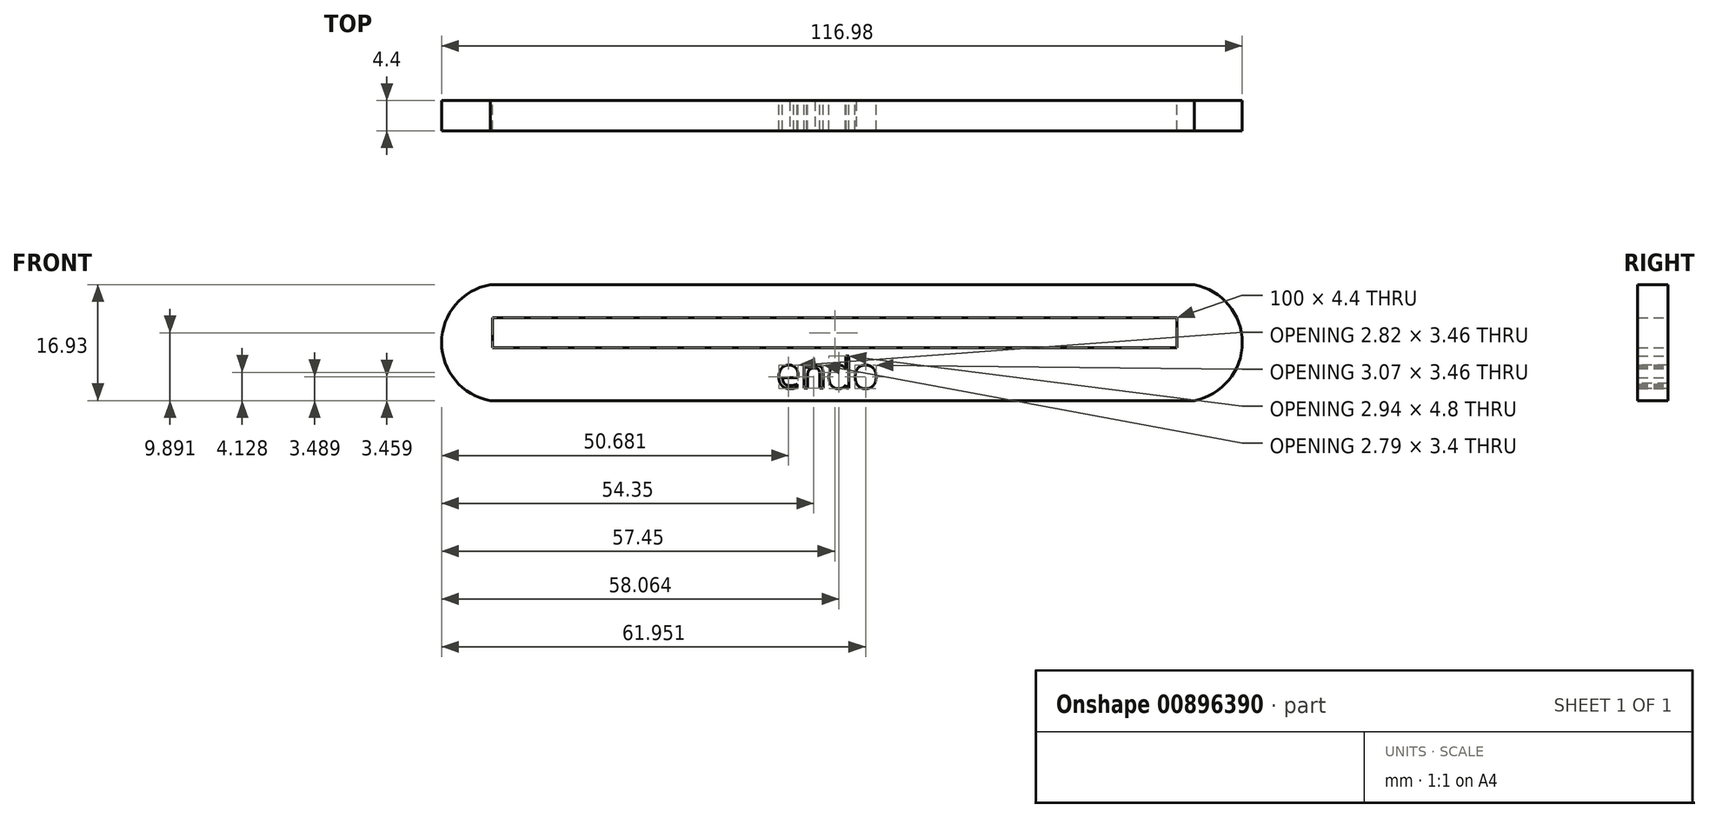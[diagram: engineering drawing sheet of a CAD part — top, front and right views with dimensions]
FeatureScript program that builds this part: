
annotation { "Feature Type Name" : "Feature", "Feature Type Description" : "" }
export const myFeature = defineFeature(function(context is Context, id is Id, definition is map)
    precondition{}
    {
        {
            var Q0;
            Q0=qCreatedBy(makeId("Front.planeOp"),FACE);
            var sketch = newSketch(context, id + "F0", { "sketchPlane" : qUnion([Q0])});
            skLineSegment(sketch, "E0", {"start": v(-14.37, 19.8) * mm, "end": v(-12.84, 20.5) * mm});
            skLineSegment(sketch, "E1", {"start": v(-12.84, 20.5) * mm, "end": v(-11.5, 21.11) * mm});
            skLineSegment(sketch, "E2", {"start": v(-11.5, 21.11) * mm, "end": v(-9.6, 21.92) * mm});
            skLineSegment(sketch, "E3", {"start": v(-9.6, 21.92) * mm, "end": v(-7.78, 22.67) * mm});
            skLineSegment(sketch, "E4", {"start": v(-7.78, 22.67) * mm, "end": v(-5.32, 23.36) * mm});
            skLineSegment(sketch, "E5", {"start": v(-5.32, 23.36) * mm, "end": v(-3.2, 23.87) * mm});
            skLineSegment(sketch, "E6", {"start": v(-3.2, 23.87) * mm, "end": v(-0.6, 24.35) * mm});
            skLineSegment(sketch, "E7", {"start": v(-0.6, 24.35) * mm, "end": v(1.8, 24.68) * mm});
            skLineSegment(sketch, "E8", {"start": v(1.8, 24.68) * mm, "end": v(4.06, 24.68) * mm});
            skLineSegment(sketch, "E9", {"start": v(4.06, 24.68) * mm, "end": v(6.76, 24.92) * mm});
            skLineSegment(sketch, "E10", {"start": v(6.76, 24.92) * mm, "end": v(9.3, 24.92) * mm});
            skLineSegment(sketch, "E11", {"start": v(9.3, 24.92) * mm, "end": v(10.16, 24.92) * mm});
            skLineSegment(sketch, "E12", {"start": v(10.16, 24.92) * mm, "end": v(11.26, 24.92) * mm});
            skLineSegment(sketch, "E13", {"start": v(11.26, 24.92) * mm, "end": v(13.38, 24.6) * mm});
            skLineSegment(sketch, "E14", {"start": v(13.38, 24.6) * mm, "end": v(14.76, 24.3) * mm});
            skLineSegment(sketch, "E15", {"start": v(-6.2, 22.67) * mm, "end": v(-4, 20.8) * mm});
            skLineSegment(sketch, "E16", {"start": v(-4, 20.8) * mm, "end": v(-1.58, 18.38) * mm});
            skLineSegment(sketch, "E17", {"start": v(-1.58, 18.38) * mm, "end": v(0.62, 16.02) * mm});
            skLineSegment(sketch, "E18", {"start": v(0.62, 16.02) * mm, "end": v(3.16, 12.97) * mm});
            skLineSegment(sketch, "E19", {"start": v(3.16, 12.97) * mm, "end": v(5.46, 10) * mm});
            skLineSegment(sketch, "E20", {"start": v(5.46, 10) * mm, "end": v(1.36, 6.83) * mm});
            skLineSegment(sketch, "E21", {"start": v(1.36, 6.83) * mm, "end": v(-1.17, 4.9) * mm});
            skLineSegment(sketch, "E22", {"start": v(-1.17, 4.9) * mm, "end": v(-3.62, 3.1) * mm});
            skLineSegment(sketch, "E23", {"start": v(-3.62, 3.1) * mm, "end": v(-5.05, 2.17) * mm});
            skLineSegment(sketch, "E24", {"start": v(-5.05, 2.17) * mm, "end": v(-6.42, 1.76) * mm});
            skLineSegment(sketch, "E25", {"start": v(-6.42, 1.76) * mm, "end": v(-8.2, 1.4) * mm});
            skLineSegment(sketch, "E26", {"start": v(-8.2, 1.4) * mm, "end": v(-9.92, 1.4) * mm});
            skLineSegment(sketch, "E27", {"start": v(-9.92, 1.4) * mm, "end": v(-11.61, 2.17) * mm});
            skLineSegment(sketch, "E28", {"start": v(-11.61, 2.17) * mm, "end": v(-13.71, 3.28) * mm});
            skLineSegment(sketch, "E29", {"start": v(-13.71, 3.28) * mm, "end": v(-15.08, 4.24) * mm});
            skLineSegment(sketch, "E30", {"start": v(-15.08, 4.24) * mm, "end": v(-16.23, 5.16) * mm});
            skLineSegment(sketch, "E31", {"start": v(-16.23, 5.16) * mm, "end": v(-17.57, 6.44) * mm});
            skLineSegment(sketch, "E32", {"start": v(-17.57, 6.44) * mm, "end": v(-18.97, 8.25) * mm});
            skLineSegment(sketch, "E33", {"start": v(-18.97, 8.25) * mm, "end": v(-19.8, 10.26) * mm});
            skLineSegment(sketch, "E34", {"start": v(-19.8, 10.26) * mm, "end": v(-20.4, 12.58) * mm});
            skLineSegment(sketch, "E35", {"start": v(-20.4, 12.58) * mm, "end": v(-20.4, 14.43) * mm});
            skLineSegment(sketch, "E36", {"start": v(-20.4, 14.43) * mm, "end": v(-20.4, 15.39) * mm});
            skLineSegment(sketch, "E37", {"start": v(-20.4, 15.39) * mm, "end": v(-20.4, 15.77) * mm});
            skLineSegment(sketch, "E38", {"start": v(-20.4, 15.77) * mm, "end": v(-19.8, 16.21) * mm});
            skLineSegment(sketch, "E39", {"start": v(-19.8, 16.21) * mm, "end": v(-19.22, 16.66) * mm});
            skLineSegment(sketch, "E40", {"start": v(-19.22, 16.66) * mm, "end": v(-18.59, 17.1) * mm});
            skLineSegment(sketch, "E41", {"start": v(-18.59, 17.1) * mm, "end": v(-17.66, 17.62) * mm});
            skLineSegment(sketch, "E42", {"start": v(-17.66, 17.62) * mm, "end": v(-16.26, 18.41) * mm});
            skLineSegment(sketch, "E43", {"start": v(-16.26, 18.41) * mm, "end": v(-14.37, 19.4) * mm});
            skLineSegment(sketch, "E44", {"start": v(-14.37, 19.4) * mm, "end": v(-9.64, 21.53) * mm});
            skLineSegment(sketch, "E45", {"start": v(-9.64, 21.53) * mm, "end": v(-8.2, 22.19) * mm});
            skLineSegment(sketch, "E46", {"start": v(-8.2, 22.19) * mm, "end": v(-6.49, 22.71) * mm});
            skLineSegment(sketch, "E47", {"start": v(-6.49, 22.71) * mm, "end": v(-6.2, 22.67) * mm});
            skLineSegment(sketch, "E48", {"start": v(-14.37, 19.8) * mm, "end": v(-15.76, 19.8) * mm});
            skLineSegment(sketch, "E49", {"start": v(-15.76, 19.8) * mm, "end": v(-18.48, 20.24) * mm});
            skLineSegment(sketch, "E50", {"start": v(-18.48, 20.24) * mm, "end": v(-19.61, 20.24) * mm});
            skLineSegment(sketch, "E51", {"start": v(-19.61, 20.24) * mm, "end": v(-21.2, 20.24) * mm});
            skLineSegment(sketch, "E52", {"start": v(-21.2, 20.24) * mm, "end": v(-22.72, 20.24) * mm});
            skLineSegment(sketch, "E53", {"start": v(-22.72, 20.24) * mm, "end": v(-24.16, 20) * mm});
            skLineSegment(sketch, "E54", {"start": v(-24.16, 20) * mm, "end": v(-25.7, 19.62) * mm});
            skLineSegment(sketch, "E55", {"start": v(-25.7, 19.62) * mm, "end": v(-27.35, 19.03) * mm});
            skLineSegment(sketch, "E56", {"start": v(-27.35, 19.03) * mm, "end": v(-29.07, 18.04) * mm});
            skLineSegment(sketch, "E57", {"start": v(-29.07, 18.04) * mm, "end": v(-30.32, 17.21) * mm});
            skLineSegment(sketch, "E58", {"start": v(-30.32, 17.21) * mm, "end": v(-31.56, 16.22) * mm});
            skLineSegment(sketch, "E59", {"start": v(-31.56, 16.22) * mm, "end": v(-32.9, 14.85) * mm});
            skLineSegment(sketch, "E60", {"start": v(-32.9, 14.85) * mm, "end": v(-34.29, 13.33) * mm});
            skLineSegment(sketch, "E61", {"start": v(-34.29, 13.33) * mm, "end": v(-35.55, 11.64) * mm});
            skLineSegment(sketch, "E62", {"start": v(-26.63, 12.1) * mm, "end": v(-27.14, 11.27) * mm});
            skLineSegment(sketch, "E63", {"start": v(-27.14, 11.27) * mm, "end": v(-27.86, 8.61) * mm});
            skLineSegment(sketch, "E64", {"start": v(-27.86, 8.61) * mm, "end": v(-27.86, 8.33) * mm});
            skLineSegment(sketch, "E65", {"start": v(-27.86, 8.33) * mm, "end": v(-26.42, 12.22) * mm});
            skLineSegment(sketch, "E66", {"start": v(-26.42, 12.22) * mm, "end": v(-26.63, 12.1) * mm});
            skLineSegment(sketch, "E67", {"start": v(-35.55, 11.64) * mm, "end": v(-37.65, 8.82) * mm});
            skLineSegment(sketch, "E68", {"start": v(-37.65, 8.82) * mm, "end": v(-38.58, 6.3) * mm});
            skLineSegment(sketch, "E69", {"start": v(-38.58, 6.3) * mm, "end": v(-39.61, 3.52) * mm});
            skLineSegment(sketch, "E70", {"start": v(-39.61, 3.52) * mm, "end": v(-40.12, -3.45) * mm});
            skLineSegment(sketch, "E71", {"start": v(-40.12, -3.45) * mm, "end": v(-36.66, -6.6) * mm});
            skLineSegment(sketch, "E72", {"start": v(-36.66, -6.6) * mm, "end": v(-31.38, -11.2) * mm});
            skLineSegment(sketch, "E73", {"start": v(-31.38, -11.2) * mm, "end": v(-29.18, -12.85) * mm});
            skLineSegment(sketch, "E74", {"start": v(-19.8, -1.41) * mm, "end": v(-23.14, 0) * mm});
            skLineSegment(sketch, "E75", {"start": v(-23.14, 0) * mm, "end": v(-23.14, 0.57) * mm});
            skLineSegment(sketch, "E76", {"start": v(-23.14, 0.57) * mm, "end": v(-18.73, -1.14) * mm});
            skLineSegment(sketch, "E77", {"start": v(-18.73, -1.14) * mm, "end": v(-19.8, -1.41) * mm});
            skLineSegment(sketch, "E78", {"start": v(-31.56, 16.22) * mm, "end": v(-32.59, 13.43) * mm});
            skLineSegment(sketch, "E79", {"start": v(-32.59, 13.43) * mm, "end": v(-37.24, 8.1) * mm});
            skLineSegment(sketch, "E80", {"start": v(-37.24, 8.1) * mm, "end": v(-36.3, 10.64) * mm});
            skLineSegment(sketch, "E81", {"start": v(-28.86, -9.02) * mm, "end": v(-27.82, -8.4) * mm});
            skLineSegment(sketch, "E82", {"start": v(-27.82, -8.4) * mm, "end": v(-25.66, -7.72) * mm});
            skLineSegment(sketch, "E83", {"start": v(-25.66, -7.72) * mm, "end": v(-22.42, -6.86) * mm});
            skLineSegment(sketch, "E84", {"start": v(-22.42, -6.86) * mm, "end": v(-21.78, -6.63) * mm});
            skLineSegment(sketch, "E85", {"start": v(-21.78, -6.63) * mm, "end": v(-20.96, -6.63) * mm});
            skLineSegment(sketch, "E86", {"start": v(-20.96, -6.63) * mm, "end": v(-20.22, -6.8) * mm});
            skLineSegment(sketch, "E87", {"start": v(-20.22, -6.8) * mm, "end": v(-18.78, -7.38) * mm});
            skLineSegment(sketch, "E88", {"start": v(-18.78, -7.38) * mm, "end": v(-21.57, -9.34) * mm});
            skLineSegment(sketch, "E89", {"start": v(-21.57, -9.34) * mm, "end": v(-22.56, -9.9) * mm});
            skLineSegment(sketch, "E90", {"start": v(-22.56, -9.9) * mm, "end": v(-23.64, -10.29) * mm});
            skLineSegment(sketch, "E91", {"start": v(-23.64, -10.29) * mm, "end": v(-24.72, -10.5) * mm});
            skLineSegment(sketch, "E92", {"start": v(-24.72, -10.5) * mm, "end": v(-25.8, -10.5) * mm});
            skLineSegment(sketch, "E93", {"start": v(-25.8, -10.5) * mm, "end": v(-28.52, -9.42) * mm});
            skLineSegment(sketch, "E94", {"start": v(-28.52, -9.42) * mm, "end": v(-28.86, -9.02) * mm});
            skLineSegment(sketch, "E95", {"start": v(-36.66, -6.6) * mm, "end": v(-36.3, -7.81) * mm});
            skLineSegment(sketch, "E96", {"start": v(-36.3, -7.81) * mm, "end": v(-35.69, -9.02) * mm});
            skLineSegment(sketch, "E97", {"start": v(-35.69, -9.02) * mm, "end": v(-34, -11) * mm});
            skLineSegment(sketch, "E98", {"start": v(-34, -11) * mm, "end": v(-32.11, -12.4) * mm});
            skLineSegment(sketch, "E99", {"start": v(-32.11, -12.4) * mm, "end": v(-30.96, -13.41) * mm});
            skLineSegment(sketch, "E100", {"start": v(-30.96, -13.41) * mm, "end": v(-31.96, -14.75) * mm});
            skLineSegment(sketch, "E101", {"start": v(-31.96, -14.75) * mm, "end": v(-30.67, -16.2) * mm});
            skLineSegment(sketch, "E102", {"start": v(-30.67, -16.2) * mm, "end": v(-29.38, -17.22) * mm});
            skLineSegment(sketch, "E103", {"start": v(-29.38, -17.22) * mm, "end": v(-27.98, -18.01) * mm});
            skLineSegment(sketch, "E104", {"start": v(-27.98, -18.01) * mm, "end": v(-27.75, -18.37) * mm});
            skLineSegment(sketch, "E105", {"start": v(-27.75, -18.37) * mm, "end": v(-26.52, -18.74) * mm});
            skLineSegment(sketch, "E106", {"start": v(-26.52, -18.74) * mm, "end": v(-22.5, -19.28) * mm});
            skLineSegment(sketch, "E107", {"start": v(-22.5, -19.28) * mm, "end": v(-20.23, -19.28) * mm});
            skLineSegment(sketch, "E108", {"start": v(-20.23, -19.28) * mm, "end": v(-18.05, -19.28) * mm});
            skLineSegment(sketch, "E109", {"start": v(-18.05, -19.28) * mm, "end": v(-17.55, -19.64) * mm});
            skLineSegment(sketch, "E110", {"start": v(-17.55, -19.64) * mm, "end": v(-16.56, -19.64) * mm});
            skLineSegment(sketch, "E111", {"start": v(-16.56, -19.64) * mm, "end": v(-16.56, -18.01) * mm});
            skLineSegment(sketch, "E112", {"start": v(-16.56, -18.01) * mm, "end": v(-16.36, -18.01) * mm});
            skLineSegment(sketch, "E113", {"start": v(-16.36, -18.01) * mm, "end": v(-15.69, -19) * mm});
            skLineSegment(sketch, "E114", {"start": v(-15.69, -19) * mm, "end": v(-14.87, -19.93) * mm});
            skLineSegment(sketch, "E115", {"start": v(-14.87, -19.93) * mm, "end": v(-14, -20.56) * mm});
            skLineSegment(sketch, "E116", {"start": v(-14, -20.56) * mm, "end": v(-13.34, -20.97) * mm});
            skLineSegment(sketch, "E117", {"start": v(-13.34, -20.97) * mm, "end": v(-12.71, -21.2) * mm});
            skLineSegment(sketch, "E118", {"start": v(-12.71, -21.2) * mm, "end": v(-11.38, -21.44) * mm});
            skLineSegment(sketch, "E119", {"start": v(-11.38, -21.44) * mm, "end": v(-9.9, -21.44) * mm});
            skLineSegment(sketch, "E120", {"start": v(-9.9, -21.44) * mm, "end": v(-8.37, -20.88) * mm});
            skLineSegment(sketch, "E121", {"start": v(-8.37, -20.88) * mm, "end": v(-7.4, -20.54) * mm});
            skLineSegment(sketch, "E122", {"start": v(-7.4, -20.54) * mm, "end": v(-6.02, -19.93) * mm});
            skLineSegment(sketch, "E123", {"start": v(-6.02, -19.93) * mm, "end": v(-4.94, -19.28) * mm});
            skLineSegment(sketch, "E124", {"start": v(-4.94, -19.28) * mm, "end": v(-3.95, -18.42) * mm});
            skLineSegment(sketch, "E125", {"start": v(-3.95, -18.42) * mm, "end": v(-2.83, -17.5) * mm});
            skLineSegment(sketch, "E126", {"start": v(-2.83, -17.5) * mm, "end": v(-1.97, -16.71) * mm});
            skLineSegment(sketch, "E127", {"start": v(-1.97, -16.71) * mm, "end": v(-1.12, -15.74) * mm});
            skLineSegment(sketch, "E128", {"start": v(-1.12, -15.74) * mm, "end": v(-0.48, -14.75) * mm});
            skLineSegment(sketch, "E129", {"start": v(-0.48, -14.75) * mm, "end": v(0.21, -13.06) * mm});
            skLineSegment(sketch, "E130", {"start": v(0.21, -13.06) * mm, "end": v(0.21, -11.98) * mm});
            skLineSegment(sketch, "E131", {"start": v(0.21, -11.98) * mm, "end": v(0.15, -10.97) * mm});
            skLineSegment(sketch, "E132", {"start": v(0.15, -10.97) * mm, "end": v(-0.3, -10.05) * mm});
            skLineSegment(sketch, "E133", {"start": v(-0.3, -10.05) * mm, "end": v(-1.1, -9.75) * mm});
            skLineSegment(sketch, "E134", {"start": v(-1.1, -9.75) * mm, "end": v(-2.3, -9.5) * mm});
            skLineSegment(sketch, "E135", {"start": v(-2.3, -9.5) * mm, "end": v(-4.02, -9.5) * mm});
            skLineSegment(sketch, "E136", {"start": v(-4.02, -9.5) * mm, "end": v(-5.46, -9.87) * mm});
            skLineSegment(sketch, "E137", {"start": v(-5.46, -9.87) * mm, "end": v(-6.9, -10.4) * mm});
            skLineSegment(sketch, "E138", {"start": v(-6.9, -10.4) * mm, "end": v(-7.96, -11.01) * mm});
            skLineSegment(sketch, "E139", {"start": v(-7.96, -11.01) * mm, "end": v(-9.09, -11.62) * mm});
            skLineSegment(sketch, "E140", {"start": v(-9.09, -11.62) * mm, "end": v(-10.06, -12.39) * mm});
            skLineSegment(sketch, "E141", {"start": v(-10.06, -12.39) * mm, "end": v(-10.98, -13.27) * mm});
            skLineSegment(sketch, "E142", {"start": v(-10.98, -13.27) * mm, "end": v(-12.3, -14.98) * mm});
            skLineSegment(sketch, "E143", {"start": v(-12.3, -14.98) * mm, "end": v(-13.1, -16.35) * mm});
            skLineSegment(sketch, "E144", {"start": v(-13.1, -16.35) * mm, "end": v(-13.6, -18.42) * mm});
            skLineSegment(sketch, "E145", {"start": v(-13.6, -18.42) * mm, "end": v(-12.83, -20.76) * mm});
            skLineSegment(sketch, "E146", {"start": v(-12.83, -20.76) * mm, "end": v(-11.38, -21.44) * mm});
            skLineSegment(sketch, "E147", {"start": v(-16.36, -18.01) * mm, "end": v(-16.07, -16.45) * mm});
            skLineSegment(sketch, "E148", {"start": v(-16.07, -16.45) * mm, "end": v(-15, -14.75) * mm});
            skLineSegment(sketch, "E149", {"start": v(-15, -14.75) * mm, "end": v(-13.73, -13.56) * mm});
            skLineSegment(sketch, "E150", {"start": v(-13.73, -13.56) * mm, "end": v(-12.66, -12.83) * mm});
            skLineSegment(sketch, "E151", {"start": v(-12.66, -12.83) * mm, "end": v(-11.38, -11.97) * mm});
            skLineSegment(sketch, "E152", {"start": v(-11.38, -11.97) * mm, "end": v(-10.42, -11.31) * mm});
            skLineSegment(sketch, "E153", {"start": v(-10.42, -11.31) * mm, "end": v(-8.78, -10.2) * mm});
            skLineSegment(sketch, "E154", {"start": v(-8.78, -10.2) * mm, "end": v(-6.81, -9.41) * mm});
            skLineSegment(sketch, "E155", {"start": v(-6.81, -9.41) * mm, "end": v(-5.1, -8.8) * mm});
            skLineSegment(sketch, "E156", {"start": v(-5.1, -8.8) * mm, "end": v(-3.2, -8.1) * mm});
            skLineSegment(sketch, "E157", {"start": v(-3.2, -8.1) * mm, "end": v(-1.86, -7.84) * mm});
            skLineSegment(sketch, "E158", {"start": v(-1.86, -7.84) * mm, "end": v(0, -8.18) * mm});
            skLineSegment(sketch, "E159", {"start": v(0, -8.18) * mm, "end": v(1.43, -9.4) * mm});
            skLineSegment(sketch, "E160", {"start": v(1.43, -9.4) * mm, "end": v(1.63, -10.81) * mm});
            skLineSegment(sketch, "E161", {"start": v(1.63, -10.81) * mm, "end": v(1.9, -12.86) * mm});
            skLineSegment(sketch, "E162", {"start": v(1.9, -12.86) * mm, "end": v(1.55, -14.75) * mm});
            skLineSegment(sketch, "E163", {"start": v(1.55, -14.75) * mm, "end": v(0.31, -12.93) * mm});
            skLineSegment(sketch, "E164", {"start": v(-14, -13.8) * mm, "end": v(-17.21, -14.02) * mm});
            skPoint(sketch, "E164.startSnap0", {"position": v(1.73, -13.8) * mm});
            skLineSegment(sketch, "E165", {"start": v(-17.21, -14.02) * mm, "end": v(-16.18, -13.06) * mm});
            skLineSegment(sketch, "E166", {"start": v(-16.18, -13.06) * mm, "end": v(-14.94, -12.22) * mm});
            skLineSegment(sketch, "E167", {"start": v(-14.94, -12.22) * mm, "end": v(-13.32, -11.01) * mm});
            skLineSegment(sketch, "E168", {"start": v(-13.32, -11.01) * mm, "end": v(-11.5, -10.08) * mm});
            skLineSegment(sketch, "E169", {"start": v(-11.5, -10.08) * mm, "end": v(-8.6, -8.98) * mm});
            skLineSegment(sketch, "E170", {"start": v(-32.03, -10.64) * mm, "end": v(-29.73, -14.32) * mm});
            skLineSegment(sketch, "E171", {"start": v(-29.73, -14.32) * mm, "end": v(-28.15, -16.14) * mm});
            skLineSegment(sketch, "E172", {"start": v(-28.15, -16.14) * mm, "end": v(-26.63, -17.27) * mm});
            skLineSegment(sketch, "E173", {"start": v(-26.63, -17.27) * mm, "end": v(-24.35, -17.96) * mm});
            skLineSegment(sketch, "E174", {"start": v(-24.35, -17.96) * mm, "end": v(-22.04, -17.96) * mm});
            skLineSegment(sketch, "E175", {"start": v(-22.04, -17.96) * mm, "end": v(-20.52, -17.96) * mm});
            skLineSegment(sketch, "E176", {"start": v(-20.52, -17.96) * mm, "end": v(-20.52, -18.15) * mm});
            skLineSegment(sketch, "E177", {"start": v(-20.52, -18.15) * mm, "end": v(-19.92, -18.15) * mm});
            skLineSegment(sketch, "E178", {"start": v(-19.92, -18.15) * mm, "end": v(-19.92, -17.96) * mm});
            skLineSegment(sketch, "E179", {"start": v(-19.92, -17.96) * mm, "end": v(-16.6, -17.32) * mm});
            skLineSegment(sketch, "E180", {"start": v(-16.6, -17.32) * mm, "end": v(-16.36, -18.01) * mm});
            skLineSegment(sketch, "E181", {"start": v(-20.96, -17.96) * mm, "end": v(-16.68, -16.83) * mm});
            skLineSegment(sketch, "E182", {"start": v(-16.68, -16.83) * mm, "end": v(-16.36, -16.4) * mm});
            skLineSegment(sketch, "E183", {"start": v(-16.36, -16.4) * mm, "end": v(-21.8, -16.4) * mm});
            skLineSegment(sketch, "E184", {"start": v(-21.8, -16.4) * mm, "end": v(-22.7, -15.73) * mm});
            skLineSegment(sketch, "E185", {"start": v(-22.7, -15.73) * mm, "end": v(-23.12, -15.35) * mm});
            skLineSegment(sketch, "E186", {"start": v(-23.12, -15.35) * mm, "end": v(-26.1, -14.33) * mm});
            skLineSegment(sketch, "E187", {"start": v(-26.1, -14.33) * mm, "end": v(-29.18, -12.85) * mm});
            skLineSegment(sketch, "E188", {"start": v(-8.6, -8.98) * mm, "end": v(-5.7, -7.8) * mm});
            skLineSegment(sketch, "E189", {"start": v(-5.7, -7.8) * mm, "end": v(-3.24, -7.46) * mm});
            skLineSegment(sketch, "E190", {"start": v(-3.24, -7.46) * mm, "end": v(-1.9, -7.27) * mm});
            skLineSegment(sketch, "E191", {"start": v(-1.9, -7.27) * mm, "end": v(-0.26, -7.54) * mm});
            skLineSegment(sketch, "E192", {"start": v(-0.26, -7.54) * mm, "end": v(0.82, -8.26) * mm});
            skLineSegment(sketch, "E193", {"start": v(0.82, -8.26) * mm, "end": v(1.5, -8.98) * mm});
            skLineSegment(sketch, "E194", {"start": v(1.5, -8.98) * mm, "end": v(1.8, -9.9) * mm});
            skLineSegment(sketch, "E195", {"start": v(1.8, -9.9) * mm, "end": v(1.98, -11.15) * mm});
            skLineSegment(sketch, "E196", {"start": v(1.98, -11.15) * mm, "end": v(2.26, -13.1) * mm});
            skLineSegment(sketch, "E197", {"start": v(2.26, -13.1) * mm, "end": v(3.74, -12.35) * mm});
            skLineSegment(sketch, "E198", {"start": v(3.74, -12.35) * mm, "end": v(6.12, -11.05) * mm});
            skLineSegment(sketch, "E199", {"start": v(6.12, -11.05) * mm, "end": v(9.27, -9.5) * mm});
            skLineSegment(sketch, "E200", {"start": v(9.27, -9.5) * mm, "end": v(18.37, -5.74) * mm});
            skLineSegment(sketch, "E201", {"start": v(18.37, -5.74) * mm, "end": v(21.69, -4.65) * mm});
            skLineSegment(sketch, "E202", {"start": v(1.55, -14.75) * mm, "end": v(8.6, -11.67) * mm});
            skLineSegment(sketch, "E203", {"start": v(8.6, -11.67) * mm, "end": v(14.4, -9.55) * mm});
            skLineSegment(sketch, "E204", {"start": v(14.4, -9.55) * mm, "end": v(20, -8.02) * mm});
            skLineSegment(sketch, "E205", {"start": v(20, -8.02) * mm, "end": v(26.3, -6.44) * mm});
            skLineSegment(sketch, "E206", {"start": v(26.3, -6.44) * mm, "end": v(28.09, -6.44) * mm});
            skLineSegment(sketch, "E207", {"start": v(28.09, -6.44) * mm, "end": v(28.53, -5.36) * mm});
            skLineSegment(sketch, "E208", {"start": v(-1.91, 1.26) * mm, "end": v(-0.42, 3) * mm});
            skLineSegment(sketch, "E209", {"start": v(-0.42, 3) * mm, "end": v(1.47, 4.76) * mm});
            skLineSegment(sketch, "E210", {"start": v(1.47, 4.76) * mm, "end": v(2.7, 5.96) * mm});
            skLineSegment(sketch, "E211", {"start": v(2.7, 5.96) * mm, "end": v(4.14, 7) * mm});
            skLineSegment(sketch, "E212", {"start": v(4.14, 7) * mm, "end": v(7.13, 8.84) * mm});
            skLineSegment(sketch, "E213", {"start": v(7.13, 8.84) * mm, "end": v(9.78, 10.12) * mm});
            skLineSegment(sketch, "E214", {"start": v(9.78, 10.12) * mm, "end": v(12.36, 11.01) * mm});
            skLineSegment(sketch, "E215", {"start": v(12.36, 11.01) * mm, "end": v(14.35, 11.54) * mm});
            skLineSegment(sketch, "E216", {"start": v(14.35, 11.54) * mm, "end": v(16.1, 11.85) * mm});
            skLineSegment(sketch, "E217", {"start": v(16.1, 11.85) * mm, "end": v(17.72, 12.17) * mm});
            skLineSegment(sketch, "E218", {"start": v(17.72, 12.17) * mm, "end": v(19.92, 12.17) * mm});
            skLineSegment(sketch, "E219", {"start": v(19.92, 12.17) * mm, "end": v(22, 12.17) * mm});
            skLineSegment(sketch, "E220", {"start": v(22, 12.17) * mm, "end": v(23.46, 12.17) * mm});
            skLineSegment(sketch, "E221", {"start": v(23.46, 12.17) * mm, "end": v(25.1, 12.17) * mm});
            skLineSegment(sketch, "E222", {"start": v(25.1, 12.17) * mm, "end": v(26.96, 11.6) * mm});
            skLineSegment(sketch, "E223", {"start": v(26.96, 11.6) * mm, "end": v(26.14, 10.78) * mm});
            skLineSegment(sketch, "E224", {"start": v(26.14, 10.78) * mm, "end": v(24.38, 9.86) * mm});
            skLineSegment(sketch, "E225", {"start": v(24.38, 9.86) * mm, "end": v(22.59, 8.84) * mm});
            skLineSegment(sketch, "E226", {"start": v(22.59, 8.84) * mm, "end": v(19.92, 7.64) * mm});
            skLineSegment(sketch, "E227", {"start": v(19.92, 7.64) * mm, "end": v(17.04, 6.24) * mm});
            skLineSegment(sketch, "E228", {"start": v(17.04, 6.24) * mm, "end": v(11.34, 3.78) * mm});
            skLineSegment(sketch, "E229", {"start": v(11.34, 3.78) * mm, "end": v(6.5, 1.98) * mm});
            skLineSegment(sketch, "E230", {"start": v(6.5, 1.98) * mm, "end": v(2.32, 0.5) * mm});
            skLineSegment(sketch, "E231", {"start": v(2.32, 0.5) * mm, "end": v(-2.22, 0.7) * mm});
            skLineSegment(sketch, "E232", {"start": v(-2.22, 0.7) * mm, "end": v(-1.91, 1.26) * mm});
            skLineSegment(sketch, "E233", {"start": v(25.1, 12.17) * mm, "end": v(24.59, 9.96) * mm});
            skLineSegment(sketch, "E234", {"start": v(4.07, -6.55) * mm, "end": v(24.22, 2.8) * mm});
            skLineSegment(sketch, "E235", {"start": v(24.22, 2.8) * mm, "end": v(24.83, 3.11) * mm});
            skLineSegment(sketch, "E236", {"start": v(24.83, 3.11) * mm, "end": v(27.67, 2.77) * mm});
            skLineSegment(sketch, "E237", {"start": v(27.67, 2.77) * mm, "end": v(23.35, -2.95) * mm});
            skLineSegment(sketch, "E238", {"start": v(23.35, -2.95) * mm, "end": v(22.3, -1.13) * mm});
            skLineSegment(sketch, "E239", {"start": v(22.3, -1.13) * mm, "end": v(24.22, 2.8) * mm});
            skLineSegment(sketch, "E240", {"start": v(23.96, -2.14) * mm, "end": v(23.96, -0.79) * mm});
            skLineSegment(sketch, "E241", {"start": v(23.96, -0.79) * mm, "end": v(26.25, 2.94) * mm});
            skLineSegment(sketch, "E242", {"start": v(4.07, -6.55) * mm, "end": v(6.54, -9.61) * mm});
            skLineSegment(sketch, "E243", {"start": v(6.54, -9.61) * mm, "end": v(23.35, -2.95) * mm});
            skLineSegment(sketch, "E244", {"start": v(6.16, -9.14) * mm, "end": v(6.16, -8.55) * mm});
            skLineSegment(sketch, "E245", {"start": v(6.16, -8.55) * mm, "end": v(4.42, -6.39) * mm});
            skLineSegment(sketch, "E246", {"start": v(7.7, -10.28) * mm, "end": v(8.06, -11.03) * mm});
            skLineSegment(sketch, "E247", {"start": v(8.06, -11.03) * mm, "end": v(17.94, -7.87) * mm});
            skLineSegment(sketch, "E248", {"start": v(17.94, -7.87) * mm, "end": v(23.2, -6.4) * mm});
            skLineSegment(sketch, "E249", {"start": v(23.2, -6.4) * mm, "end": v(26.72, -5.64) * mm});
            skLineSegment(sketch, "E250", {"start": v(26.72, -5.64) * mm, "end": v(28.53, -5.36) * mm});
            skLineSegment(sketch, "E251", {"start": v(21.69, -4.65) * mm, "end": v(24.71, -4.65) * mm});
            skLineSegment(sketch, "E252", {"start": v(24.71, -4.65) * mm, "end": v(27.78, -4.65) * mm});
            skLineSegment(sketch, "E253", {"start": v(27.78, -4.65) * mm, "end": v(29.83, -2.46) * mm});
            skLineSegment(sketch, "E254", {"start": v(29.83, -2.46) * mm, "end": v(32.9, 1.18) * mm});
            skLineSegment(sketch, "E255", {"start": v(32.9, 1.18) * mm, "end": v(35.47, 3.45) * mm});
            skLineSegment(sketch, "E256", {"start": v(35.47, 3.45) * mm, "end": v(37.69, 4.54) * mm});
            skLineSegment(sketch, "E257", {"start": v(37.69, 4.54) * mm, "end": v(39.57, 5.29) * mm});
            skLineSegment(sketch, "E258", {"start": v(39.57, 5.29) * mm, "end": v(40.13, 5.29) * mm});
            skLineSegment(sketch, "E259", {"start": v(40.13, 5.29) * mm, "end": v(40.38, 4.77) * mm});
            skLineSegment(sketch, "E260", {"start": v(40.38, 4.77) * mm, "end": v(40.38, 3.26) * mm});
            skLineSegment(sketch, "E261", {"start": v(40.38, 3.26) * mm, "end": v(44.3, 9.02) * mm});
            skLineSegment(sketch, "E262", {"start": v(44.3, 9.02) * mm, "end": v(40.47, 13.26) * mm});
            skLineSegment(sketch, "E263", {"start": v(40.47, 13.26) * mm, "end": v(39.18, 13.68) * mm});
            skLineSegment(sketch, "E264", {"start": v(39.18, 13.68) * mm, "end": v(38.83, 14.4) * mm});
            skLineSegment(sketch, "E265", {"start": v(38.83, 14.4) * mm, "end": v(38.6, 15.11) * mm});
            skLineSegment(sketch, "E266", {"start": v(38.6, 15.11) * mm, "end": v(38.14, 16.47) * mm});
            skLineSegment(sketch, "E267", {"start": v(38.14, 16.47) * mm, "end": v(31.87, 21.74) * mm});
            skLineSegment(sketch, "E268", {"start": v(31.87, 21.74) * mm, "end": v(29.1, 21.74) * mm});
            skLineSegment(sketch, "E269", {"start": v(29.1, 21.74) * mm, "end": v(25.81, 23.49) * mm});
            skLineSegment(sketch, "E270", {"start": v(4.07, -6.55) * mm, "end": v(2.42, -5.14) * mm});
            skLineSegment(sketch, "E271", {"start": v(2.42, -5.14) * mm, "end": v(1.33, -4.22) * mm});
            skLineSegment(sketch, "E272", {"start": v(1.33, -4.22) * mm, "end": v(-1.8, -4.22) * mm});
            skLineSegment(sketch, "E273", {"start": v(-1.8, -4.22) * mm, "end": v(-5.73, -5.19) * mm});
            skLineSegment(sketch, "E274", {"start": v(-5.73, -5.19) * mm, "end": v(-12.25, -7.31) * mm});
            skLineSegment(sketch, "E275", {"start": v(-12.25, -7.31) * mm, "end": v(-17.25, -10.42) * mm});
            skLineSegment(sketch, "E276", {"start": v(-17.25, -10.42) * mm, "end": v(-21.12, -13.64) * mm});
            skLineSegment(sketch, "E277", {"start": v(-21.12, -13.64) * mm, "end": v(-22.24, -16.07) * mm});
            skLineSegment(sketch, "E278", {"start": v(39.34, 9.96) * mm, "end": v(38.28, 11.47) * mm});
            skLineSegment(sketch, "E279", {"start": v(38.28, 11.47) * mm, "end": v(36.99, 12.84) * mm});
            skLineSegment(sketch, "E280", {"start": v(36.99, 12.84) * mm, "end": v(37.63, 13.45) * mm});
            skPoint(sketch, "E280.endSnap0", {"position": v(37.63, 12.16) * mm});
            skLineSegment(sketch, "E281", {"start": v(37.63, 13.45) * mm, "end": v(39.34, 12.3) * mm});
            skLineSegment(sketch, "E282", {"start": v(39.34, 12.3) * mm, "end": v(40.5, 10.45) * mm});
            skLineSegment(sketch, "E283", {"start": v(40.5, 10.45) * mm, "end": v(39.99, 9.96) * mm});
            skLineSegment(sketch, "E284", {"start": v(39.99, 9.96) * mm, "end": v(39.34, 9.96) * mm});
            skLineSegment(sketch, "E285", {"start": v(40.82, 9.96) * mm, "end": v(41.61, 10.29) * mm});
            skLineSegment(sketch, "E286", {"start": v(41.61, 10.29) * mm, "end": v(40.9, 11.67) * mm});
            skLineSegment(sketch, "E287", {"start": v(40.9, 11.67) * mm, "end": v(39.73, 13.04) * mm});
            skLineSegment(sketch, "E288", {"start": v(39.73, 13.04) * mm, "end": v(39.34, 13.3) * mm});
            skLineSegment(sketch, "E289", {"start": v(39.34, 13.3) * mm, "end": v(38.8, 13.04) * mm});
            skLineSegment(sketch, "E290", {"start": v(38.8, 13.04) * mm, "end": v(39.34, 12.3) * mm});
            skLineSegment(sketch, "E291", {"start": v(40.82, 9.96) * mm, "end": v(40.5, 10.45) * mm});
            skLineSegment(sketch, "E292", {"start": v(41.9, 9.96) * mm, "end": v(42.62, 10.29) * mm});
            skLineSegment(sketch, "E293", {"start": v(42.62, 10.29) * mm, "end": v(40.4, 12.93) * mm});
            skLineSegment(sketch, "E294", {"start": v(40.4, 12.93) * mm, "end": v(39.83, 12.93) * mm});
            skLineSegment(sketch, "E295", {"start": v(41.9, 9.96) * mm, "end": v(41.61, 10.29) * mm});
            skLineSegment(sketch, "E296", {"start": v(36.24, 13.7) * mm, "end": v(30.02, 12.54) * mm});
            skLineSegment(sketch, "E297", {"start": v(10.16, 24.92) * mm, "end": v(11.64, 25.35) * mm});
            skLineSegment(sketch, "E298", {"start": v(11.64, 25.35) * mm, "end": v(13.38, 25.58) * mm});
            skLineSegment(sketch, "E299", {"start": v(13.38, 25.58) * mm, "end": v(15.35, 25.69) * mm});
            skLineSegment(sketch, "E300", {"start": v(15.35, 25.69) * mm, "end": v(18.4, 25.69) * mm});
            skLineSegment(sketch, "E301", {"start": v(18.4, 25.69) * mm, "end": v(20.4, 25.51) * mm});
            skLineSegment(sketch, "E302", {"start": v(20.4, 25.51) * mm, "end": v(20.82, 25.89) * mm});
            skLineSegment(sketch, "E303", {"start": v(20.82, 25.89) * mm, "end": v(21.61, 25.77) * mm});
            skLineSegment(sketch, "E304", {"start": v(21.61, 25.77) * mm, "end": v(22.67, 25.47) * mm});
            skLineSegment(sketch, "E305", {"start": v(22.67, 25.47) * mm, "end": v(23.05, 25.22) * mm});
            skLineSegment(sketch, "E306", {"start": v(23.05, 25.22) * mm, "end": v(23.43, 24.8) * mm});
            skLineSegment(sketch, "E307", {"start": v(23.43, 24.8) * mm, "end": v(22.95, 24.52) * mm});
            skLineSegment(sketch, "E308", {"start": v(22.95, 24.52) * mm, "end": v(20.48, 25.58) * mm});
            skLineSegment(sketch, "E309", {"start": v(24.19, 24.15) * mm, "end": v(25.08, 24.39) * mm});
            skLineSegment(sketch, "E310", {"start": v(25.08, 24.39) * mm, "end": v(24.25, 24.87) * mm});
            skLineSegment(sketch, "E311", {"start": v(24.25, 24.87) * mm, "end": v(23.05, 25.22) * mm});
            skLineSegment(sketch, "E312", {"start": v(21.41, 19.93) * mm, "end": v(19.3, 21.67) * mm});
            skLineSegment(sketch, "E313", {"start": v(19.3, 21.67) * mm, "end": v(19.86, 21.67) * mm});
            skLineSegment(sketch, "E314", {"start": v(19.86, 21.67) * mm, "end": v(22.17, 19.81) * mm});
            skLineSegment(sketch, "E315", {"start": v(22.17, 19.81) * mm, "end": v(21.49, 19.9) * mm});
            skLineSegment(sketch, "E316", {"start": v(26.1, 17.7) * mm, "end": v(30.84, 18.15) * mm});
            skLineSegment(sketch, "E317", {"start": v(30.84, 18.15) * mm, "end": v(26.96, 21.27) * mm});
            skLineSegment(sketch, "E318", {"start": v(26.96, 21.27) * mm, "end": v(19.65, 22.81) * mm});
            skLineSegment(sketch, "E319", {"start": v(19.65, 22.81) * mm, "end": v(18.52, 23.72) * mm});
            skLineSegment(sketch, "E320", {"start": v(18.52, 23.72) * mm, "end": v(19.48, 23.52) * mm});
            skLineSegment(sketch, "E321", {"start": v(19.48, 23.52) * mm, "end": v(20.62, 22.6) * mm});
            skLineSegment(sketch, "E322", {"start": v(20.62, 22.6) * mm, "end": v(24.05, 22.22) * mm});
            skLineSegment(sketch, "E323", {"start": v(24.05, 22.22) * mm, "end": v(23.75, 22.89) * mm});
            skLineSegment(sketch, "E324", {"start": v(23.75, 22.89) * mm, "end": v(22.78, 23.28) * mm});
            skLineSegment(sketch, "E325", {"start": v(22.78, 23.28) * mm, "end": v(19.48, 23.52) * mm});
            skLineSegment(sketch, "E326", {"start": v(23.75, 22.89) * mm, "end": v(24.56, 22.89) * mm});
            skLineSegment(sketch, "E327", {"start": v(24.56, 22.89) * mm, "end": v(27.91, 20.95) * mm});
            skLineSegment(sketch, "E328", {"start": v(27.91, 20.95) * mm, "end": v(25.01, 22.01) * mm});
            skLineSegment(sketch, "E329", {"start": v(25.01, 22.01) * mm, "end": v(25.01, 22.28) * mm});
            skLineSegment(sketch, "E330", {"start": v(25.01, 22.28) * mm, "end": v(24.05, 22.22) * mm});
            skLineSegment(sketch, "E331", {"start": v(26.1, 17.7) * mm, "end": v(27.97, 15.5) * mm});
            skLineSegment(sketch, "E332", {"start": v(27.97, 15.5) * mm, "end": v(30.4, 14.6) * mm});
            skLineSegment(sketch, "E333", {"start": v(30.4, 14.6) * mm, "end": v(30.44, 14.27) * mm});
            skLineSegment(sketch, "E334", {"start": v(30.44, 14.27) * mm, "end": v(32.83, 14.74) * mm});
            skLineSegment(sketch, "E335", {"start": v(32.83, 14.74) * mm, "end": v(34.39, 14.74) * mm});
            skLineSegment(sketch, "E336", {"start": v(34.39, 14.74) * mm, "end": v(35.58, 14.49) * mm});
            skLineSegment(sketch, "E337", {"start": v(35.58, 14.49) * mm, "end": v(36.99, 13.97) * mm});
            skLineSegment(sketch, "E338", {"start": v(36.99, 13.97) * mm, "end": v(37.94, 13.77) * mm});
            skLineSegment(sketch, "E339", {"start": v(37.94, 13.77) * mm, "end": v(38.52, 15.35) * mm});
            skLineSegment(sketch, "E340", {"start": v(25.81, 23.49) * mm, "end": v(26.43, 23.68) * mm});
            skLineSegment(sketch, "E341", {"start": v(26.43, 23.68) * mm, "end": v(25.08, 24.39) * mm});
            skLineSegment(sketch, "E342", {"start": v(24.19, 24.15) * mm, "end": v(22.95, 24.52) * mm});
            skLineSegment(sketch, "E343", {"start": v(25.81, 23.49) * mm, "end": v(24.19, 24.15) * mm});
            skLineSegment(sketch, "E344", {"start": v(37.27, 13.91) * mm, "end": v(37.56, 15.27) * mm});
            skLineSegment(sketch, "E345", {"start": v(37.56, 15.27) * mm, "end": v(35.5, 15.74) * mm});
            skLineSegment(sketch, "E346", {"start": v(35.5, 15.74) * mm, "end": v(35.22, 15.74) * mm});
            skLineSegment(sketch, "E347", {"start": v(35.22, 15.74) * mm, "end": v(33.25, 15.84) * mm});
            skLineSegment(sketch, "E348", {"start": v(33.25, 15.84) * mm, "end": v(33.27, 16.67) * mm});
            skLineSegment(sketch, "E349", {"start": v(33.27, 16.67) * mm, "end": v(32.7, 16.8) * mm});
            skLineSegment(sketch, "E350", {"start": v(32.7, 16.8) * mm, "end": v(32.7, 17.37) * mm});
            skLineSegment(sketch, "E351", {"start": v(32.7, 17.37) * mm, "end": v(32.25, 17.85) * mm});
            skLineSegment(sketch, "E352", {"start": v(32.25, 17.85) * mm, "end": v(31.18, 18.7) * mm});
            skLineSegment(sketch, "E353", {"start": v(31.18, 18.7) * mm, "end": v(31.85, 18.77) * mm});
            skLineSegment(sketch, "E354", {"start": v(31.85, 18.77) * mm, "end": v(32.07, 19.2) * mm});
            skLineSegment(sketch, "E355", {"start": v(32.07, 19.2) * mm, "end": v(31.17, 19.67) * mm});
            skLineSegment(sketch, "E356", {"start": v(31.8, 17.2) * mm, "end": v(31.8, 17.64) * mm});
            skLineSegment(sketch, "E357", {"start": v(31.8, 17.64) * mm, "end": v(30.64, 18.73) * mm});
            skLineSegment(sketch, "E358", {"start": v(30.64, 18.73) * mm, "end": v(30.84, 18.15) * mm});
            skLineSegment(sketch, "E359", {"start": v(31.8, 17.64) * mm, "end": v(27.3, 17.33) * mm});
            skLineSegment(sketch, "E360", {"start": v(27.3, 17.33) * mm, "end": v(28.54, 15.87) * mm});
            skLineSegment(sketch, "E361", {"start": v(28.54, 15.87) * mm, "end": v(29.82, 15.4) * mm});
            skLineSegment(sketch, "E362", {"start": v(29.82, 15.4) * mm, "end": v(32.21, 15.04) * mm});
            skLineSegment(sketch, "E363", {"start": v(32.21, 15.04) * mm, "end": v(33.12, 15.1) * mm});
            skLineSegment(sketch, "E364", {"start": v(33.12, 15.1) * mm, "end": v(32.7, 16.8) * mm});
            skLineSegment(sketch, "E365", {"start": v(30.3, 19.25) * mm, "end": v(30.75, 19.3) * mm});
            skLineSegment(sketch, "E366", {"start": v(30.75, 19.3) * mm, "end": v(30.82, 19.54) * mm});
            skLineSegment(sketch, "E367", {"start": v(30.82, 19.54) * mm, "end": v(30.36, 19.67) * mm});
            skLineSegment(sketch, "E368", {"start": v(30.36, 19.67) * mm, "end": v(29.48, 19.86) * mm});
            skLineSegment(sketch, "E369", {"start": v(31.82, 20.41) * mm, "end": v(36, 17.24) * mm});
            skLineSegment(sketch, "E370", {"start": v(36, 17.24) * mm, "end": v(36.39, 16.69) * mm});
            skLineSegment(sketch, "E371", {"start": v(36.39, 16.69) * mm, "end": v(36.16, 15.6) * mm});
            skLineSegment(sketch, "E372", {"start": v(33.77, 16.1) * mm, "end": v(34.01, 16.4) * mm});
            skLineSegment(sketch, "E373", {"start": v(34.06, 16.06) * mm, "end": v(34.24, 16.34) * mm});
            skPoint(sketch, "E373.endSnap0", {"position": v(34.24, 15.8) * mm});
            skLineSegment(sketch, "E374", {"start": v(-12.47, -18.04) * mm, "end": v(-12.16, -16.76) * mm});
            skLineSegment(sketch, "E375", {"start": v(-12.16, -16.76) * mm, "end": v(-11.32, -15.15) * mm});
            skLineSegment(sketch, "E376", {"start": v(-11.32, -15.15) * mm, "end": v(-9.54, -13.42) * mm});
            skLineSegment(sketch, "E377", {"start": v(-9.54, -13.42) * mm, "end": v(-7.15, -11.8) * mm});
            skLineSegment(sketch, "E378", {"start": v(-7.15, -11.8) * mm, "end": v(-5.01, -11.03) * mm});
            skLineSegment(sketch, "E379", {"start": v(-5.01, -11.03) * mm, "end": v(-3.21, -10.94) * mm});
            skLineSegment(sketch, "E380", {"start": v(-3.21, -10.94) * mm, "end": v(-1.96, -11.24) * mm});
            skLineSegment(sketch, "E381", {"start": v(-1.96, -11.24) * mm, "end": v(-1.28, -12.16) * mm});
            skLineSegment(sketch, "E382", {"start": v(-1.28, -12.16) * mm, "end": v(-1.25, -13.58) * mm});
            skLineSegment(sketch, "E383", {"start": v(-1.25, -13.58) * mm, "end": v(-1.88, -15.06) * mm});
            skLineSegment(sketch, "E384", {"start": v(-1.88, -15.06) * mm, "end": v(-2.92, -16.44) * mm});
            skLineSegment(sketch, "E385", {"start": v(-2.92, -16.44) * mm, "end": v(-4.2, -17.74) * mm});
            skLineSegment(sketch, "E386", {"start": v(-4.2, -17.74) * mm, "end": v(-6.12, -19.03) * mm});
            skLineSegment(sketch, "E387", {"start": v(-6.12, -19.03) * mm, "end": v(-8.8, -20.17) * mm});
            skLineSegment(sketch, "E388", {"start": v(-8.8, -20.17) * mm, "end": v(-11.1, -20.06) * mm});
            skLineSegment(sketch, "E389", {"start": v(-11.1, -20.06) * mm, "end": v(-12.1, -19.16) * mm});
            skLineSegment(sketch, "E390", {"start": v(-12.1, -19.16) * mm, "end": v(-12.47, -18.04) * mm});
            skLineSegment(sketch, "E391", {"start": v(-4.2, -17.74) * mm, "end": v(-6.6, -15.31) * mm});
            skLineSegment(sketch, "E392", {"start": v(-6.6, -15.31) * mm, "end": v(-6.98, -15.48) * mm});
            skLineSegment(sketch, "E393", {"start": v(-6.98, -15.48) * mm, "end": v(-7.77, -15.82) * mm});
            skLineSegment(sketch, "E394", {"start": v(-7.77, -15.82) * mm, "end": v(-9.16, -18.9) * mm});
            skLineSegment(sketch, "E395", {"start": v(-11.01, -18.04) * mm, "end": v(-8.65, -15.9) * mm});
            skLineSegment(sketch, "E396", {"start": v(-8.65, -15.9) * mm, "end": v(-12.16, -16.76) * mm});
            skLineSegment(sketch, "E397", {"start": v(-10.83, -14.67) * mm, "end": v(-9, -14.67) * mm});
            skLineSegment(sketch, "E398", {"start": v(-9, -14.67) * mm, "end": v(-8.38, -14.06) * mm});
            skLineSegment(sketch, "E399", {"start": v(-8.38, -14.06) * mm, "end": v(-8.38, -12.63) * mm});
            skLineSegment(sketch, "E400", {"start": v(-7.15, -11.8) * mm, "end": v(-6.67, -13.15) * mm});
            skLineSegment(sketch, "E401", {"start": v(-6.67, -13.15) * mm, "end": v(-3.44, -10.95) * mm});
            skLineSegment(sketch, "E402", {"start": v(-1.28, -12.16) * mm, "end": v(-5.57, -13.98) * mm});
            skLineSegment(sketch, "E403", {"start": v(-5.57, -13.98) * mm, "end": v(-5.92, -14.6) * mm});
            skLineSegment(sketch, "E404", {"start": v(-5.92, -14.6) * mm, "end": v(-2.92, -16.44) * mm});
            skLineSegment(sketch, "E405", {"start": v(-9.16, -18.9) * mm, "end": v(-9.95, -20.12) * mm});
            skLineSegment(sketch, "E406", {"start": v(-11.01, -18.04) * mm, "end": v(-12.1, -19.16) * mm});
            skLineSegment(sketch, "E407", {"start": v(-7.77, -14.64) * mm, "end": v(-7.17, -13.97) * mm});
            skLineSegment(sketch, "E408", {"start": v(-7.17, -13.97) * mm, "end": v(-6.62, -14.22) * mm});
            skLineSegment(sketch, "E409", {"start": v(-6.62, -14.22) * mm, "end": v(-6.62, -14.62) * mm});
            skLineSegment(sketch, "E410", {"start": v(-6.62, -14.62) * mm, "end": v(-7.77, -15.4) * mm});
            skLineSegment(sketch, "E411", {"start": v(-7.77, -15.4) * mm, "end": v(-7.77, -14.64) * mm});
            skLineSegment(sketch, "E412", {"start": v(28.7, -5.28) * mm, "end": v(29.45, -5.9) * mm});
            skLineSegment(sketch, "E413", {"start": v(29.45, -5.9) * mm, "end": v(31.38, -6.47) * mm});
            skLineSegment(sketch, "E414", {"start": v(31.38, -6.47) * mm, "end": v(33.86, -5.92) * mm});
            skLineSegment(sketch, "E415", {"start": v(33.86, -5.92) * mm, "end": v(36.13, -4.33) * mm});
            skLineSegment(sketch, "E416", {"start": v(36.13, -4.33) * mm, "end": v(39.01, -1.05) * mm});
            skLineSegment(sketch, "E417", {"start": v(39.01, -1.05) * mm, "end": v(40.13, 1.64) * mm});
            skLineSegment(sketch, "E418", {"start": v(40.13, 1.64) * mm, "end": v(40.32, 3.38) * mm});
            skLineSegment(sketch, "E419", {"start": v(28.53, -5.36) * mm, "end": v(28.7, -5.28) * mm});
            skLineSegment(sketch, "E420", {"start": v(28.7, -5.28) * mm, "end": v(29.68, -3.65) * mm});
            skLineSegment(sketch, "E421", {"start": v(29.68, -3.65) * mm, "end": v(31.91, -0.71) * mm});
            skLineSegment(sketch, "E422", {"start": v(31.91, -0.71) * mm, "end": v(34.1, 1.48) * mm});
            skLineSegment(sketch, "E423", {"start": v(34.1, 1.48) * mm, "end": v(36.3, 3.28) * mm});
            skLineSegment(sketch, "E424", {"start": v(36.3, 3.28) * mm, "end": v(38.73, 4.51) * mm});
            skLineSegment(sketch, "E425", {"start": v(38.73, 4.51) * mm, "end": v(39.37, 4.51) * mm});
            skLineSegment(sketch, "E426", {"start": v(39.37, 4.51) * mm, "end": v(40.38, 4.02) * mm});
            skLineSegment(sketch, "E427", {"start": v(32.06, -3.82) * mm, "end": v(33, -2.42) * mm});
            skLineSegment(sketch, "E428", {"start": v(33, -2.42) * mm, "end": v(32.18, -2.76) * mm});
            skLineSegment(sketch, "E429", {"start": v(32.18, -2.76) * mm, "end": v(32.92, -1.41) * mm});
            skLineSegment(sketch, "E430", {"start": v(32.92, -1.41) * mm, "end": v(33.35, -1.24) * mm});
            skLineSegment(sketch, "E431", {"start": v(33.35, -1.24) * mm, "end": v(33.9, -0.3) * mm});
            skLineSegment(sketch, "E432", {"start": v(33.9, -0.3) * mm, "end": v(34.5, -0.18) * mm});
            skLineSegment(sketch, "E433", {"start": v(34.5, -0.18) * mm, "end": v(34.5, 0.56) * mm});
            skLineSegment(sketch, "E434", {"start": v(34.5, 0.56) * mm, "end": v(35.07, 0.9) * mm});
            skLineSegment(sketch, "E435", {"start": v(35.07, 0.9) * mm, "end": v(35.07, 0.21) * mm});
            skLineSegment(sketch, "E436", {"start": v(35.07, 0.21) * mm, "end": v(37.27, 2.1) * mm});
            skLineSegment(sketch, "E437", {"start": v(37.27, 2.1) * mm, "end": v(38.45, 2.1) * mm});
            skLineSegment(sketch, "E438", {"start": v(38.45, 2.1) * mm, "end": v(35.57, -0.28) * mm});
            skLineSegment(sketch, "E439", {"start": v(35.57, -0.28) * mm, "end": v(35.57, -0.66) * mm});
            skLineSegment(sketch, "E440", {"start": v(35.57, -0.66) * mm, "end": v(36.85, -0.6) * mm});
            skLineSegment(sketch, "E441", {"start": v(36.85, -0.6) * mm, "end": v(37.29, -0.9) * mm});
            skLineSegment(sketch, "E442", {"start": v(37.29, -0.9) * mm, "end": v(37.29, -1.66) * mm});
            skLineSegment(sketch, "E443", {"start": v(37.29, -1.66) * mm, "end": v(36.93, -2.13) * mm});
            skLineSegment(sketch, "E444", {"start": v(36.93, -2.13) * mm, "end": v(35.1, -1.26) * mm});
            skLineSegment(sketch, "E445", {"start": v(35.1, -1.26) * mm, "end": v(34.41, -1.7) * mm});
            skLineSegment(sketch, "E446", {"start": v(34.41, -1.7) * mm, "end": v(33.26, -4.78) * mm});
            skLineSegment(sketch, "E447", {"start": v(33.26, -4.78) * mm, "end": v(32.06, -3.82) * mm});
            skLineSegment(sketch, "E448", {"start": v(33.28, -5.03) * mm, "end": v(32.33, -5.4) * mm});
            skLineSegment(sketch, "E449", {"start": v(32.33, -5.4) * mm, "end": v(31.53, -4.69) * mm});
            skLineSegment(sketch, "E450", {"start": v(31.53, -4.69) * mm, "end": v(31.8, -3.33) * mm});
            skLineSegment(sketch, "E451", {"start": v(31.8, -3.33) * mm, "end": v(32.92, -1.41) * mm});
            skLineSegment(sketch, "E452", {"start": v(32.92, -1.41) * mm, "end": v(33.4, -0.47) * mm});
            skLineSegment(sketch, "E453", {"start": v(33.4, -0.47) * mm, "end": v(34.5, 0.56) * mm});
            skLineSegment(sketch, "E454", {"start": v(35.07, 0.9) * mm, "end": v(35.72, 1.43) * mm});
            skLineSegment(sketch, "E455", {"start": v(35.72, 1.43) * mm, "end": v(36.72, 2.01) * mm});
            skLineSegment(sketch, "E456", {"start": v(36.72, 2.01) * mm, "end": v(37.27, 2.1) * mm});
            skLineSegment(sketch, "E457", {"start": v(38.45, 2.1) * mm, "end": v(39.08, 1.34) * mm});
            skLineSegment(sketch, "E458", {"start": v(39.08, 1.34) * mm, "end": v(38.77, 0) * mm});
            skLineSegment(sketch, "E459", {"start": v(38.77, 0) * mm, "end": v(37.89, -1.16) * mm});
            skLineSegment(sketch, "E460", {"start": v(37.89, -1.16) * mm, "end": v(37.02, -2.55) * mm});
            skLineSegment(sketch, "E461", {"start": v(37.02, -2.55) * mm, "end": v(35.87, -3.82) * mm});
            skLineSegment(sketch, "E462", {"start": v(35.87, -3.82) * mm, "end": v(34.5, -4.52) * mm});
            skLineSegment(sketch, "E463", {"start": v(34.5, -4.52) * mm, "end": v(33.28, -5.03) * mm});
            skLineSegment(sketch, "E464.bottom", {"start": v(45, -27.5) * mm, "end": v(-45, -27.5) * mm});
            skLineSegment(sketch, "E464.top", {"start": v(45, 27.5) * mm, "end": v(-45, 27.5) * mm});
            skLineSegment(sketch, "E464.left", {"start": v(50, -22.5) * mm, "end": v(50, 22.5) * mm});
            skLineSegment(sketch, "E464.right", {"start": v(-50, -22.5) * mm, "end": v(-50, 22.5) * mm});
            skPoint(sketch, "E464.middle", {"position": v(0, 0) * mm});
            skLineSegment(sketch, "E465", {"start": v(-50.34, -35.33) * mm, "end": v(52.52, -35.33) * mm});
            skLineSegment(sketch, "E466", {"start": v(52.52, -52.26) * mm, "end": v(-50.34, -52.26) * mm});
            skLineSegment(sketch, "E467.bottom", {"start": v(-50, -40.17) * mm, "end": v(50, -40.17) * mm});
            skLineSegment(sketch, "E467.top", {"start": v(-50, -44.57) * mm, "end": v(50, -44.57) * mm});
            skLineSegment(sketch, "E467.left", {"start": v(-50, -40.17) * mm, "end": v(-50, -44.57) * mm});
            skLineSegment(sketch, "E467.right", {"start": v(50, -40.17) * mm, "end": v(50, -44.57) * mm});
            skArc(sketch, "E468", {"start": v(-50.34, -35.33) * mm, "mid": v(-57.45, -43.8) * mm, "end": v(-50.34, -52.26) * mm});
            skArc(sketch, "E469", {"start": v(52.52, -52.26) * mm, "mid": v(59.53, -43.8) * mm, "end": v(52.52, -35.33) * mm});
            skText(sketch, "E470", { "text": "endo\n", "fontName": "OpenSans-Regular.ttf"});
            skPoint(sketch, "E471.visualSharp", {"position": v(-50, 27.5) * mm});
            skArc(sketch, "E471.filletArc", {"start": v(-45, 27.5) * mm, "mid": v(-48.54, 26.04) * mm, "end": v(-50, 22.5) * mm});
            skPoint(sketch, "E472.visualSharp", {"position": v(-50, -27.5) * mm});
            skArc(sketch, "E472.filletArc", {"start": v(-50, -22.5) * mm, "mid": v(-48.54, -26.04) * mm, "end": v(-45, -27.5) * mm});
            skPoint(sketch, "E473.visualSharp", {"position": v(50, -27.5) * mm});
            skArc(sketch, "E473.filletArc", {"start": v(45, -27.5) * mm, "mid": v(48.54, -26.04) * mm, "end": v(50, -22.5) * mm});
            skPoint(sketch, "E474.visualSharp", {"position": v(50, 27.5) * mm});
            skArc(sketch, "E474.filletArc", {"start": v(50, 22.5) * mm, "mid": v(48.54, 26.04) * mm, "end": v(45, 27.5) * mm});
            const initialGuessF0  = {"E470": [-0.00853, -0.05047, 1, 0, 0.00449]};
            skSetInitialGuess(sketch, initialGuessF0);
            skSolve(sketch);
        }
        {
            var Q0;
            Q0=makeQuery(id+"F0.imprint","IMPRINT",FACE,{"disambiguationData":[TD([[makeQuery(id+"F0.imprint","IMPRINT",EDGE,{"derivedFrom":sQuery(id+"F0.wireOp",EDGE,"E465")}),-1.0]])]});
            extrude(context, id + "F1", {"entities" : qUnion([Q0]), "depth" : 4.4 * mm, "offsetDistance" : 25 * mm});
        }
    });
